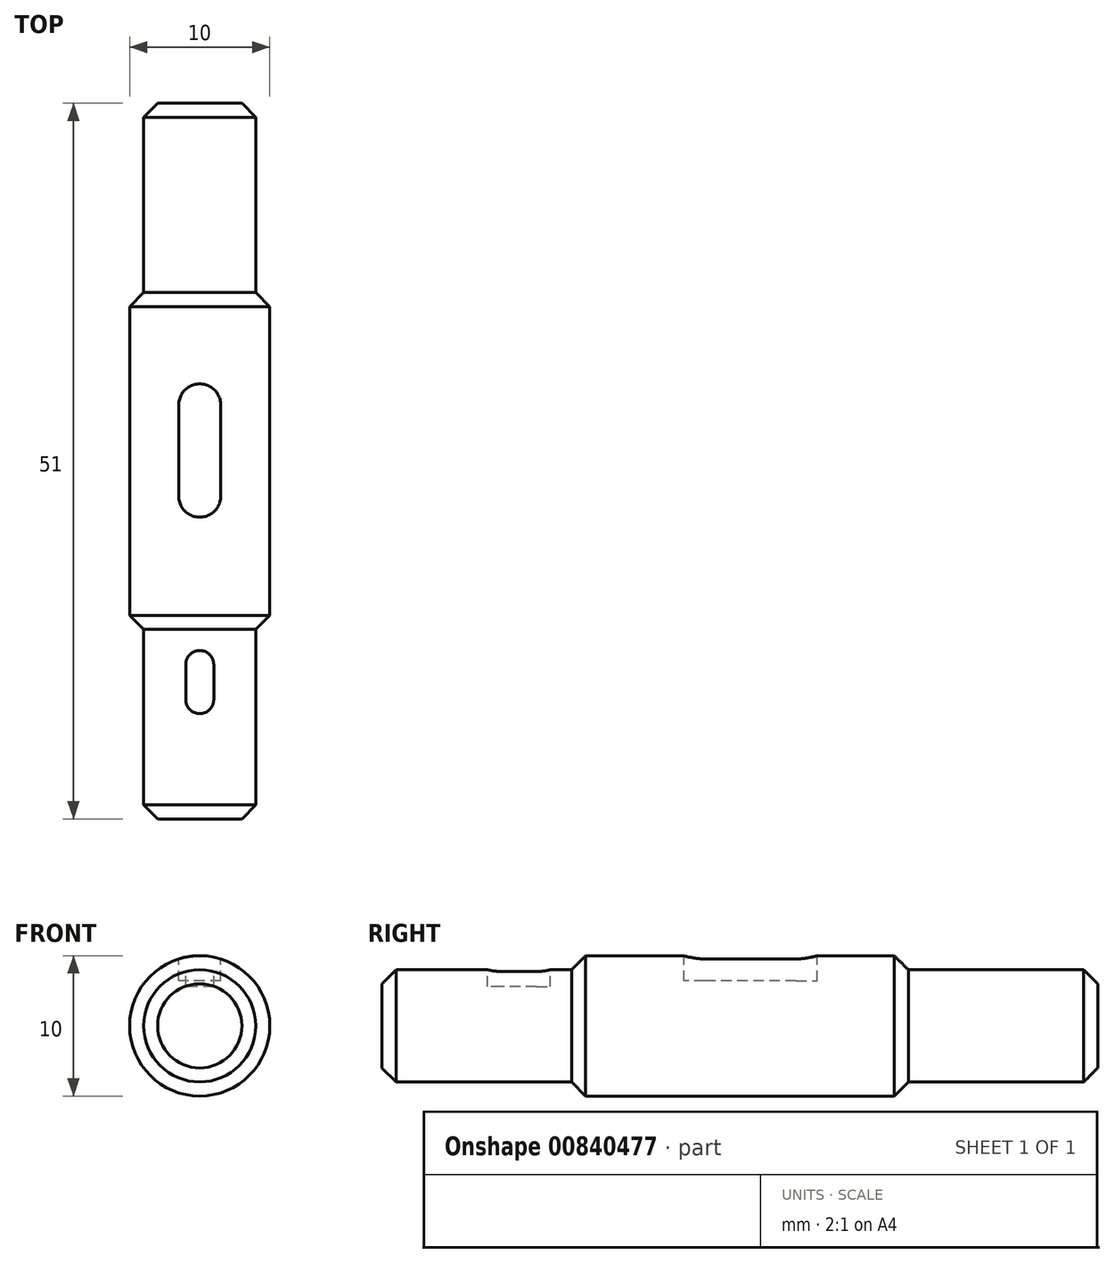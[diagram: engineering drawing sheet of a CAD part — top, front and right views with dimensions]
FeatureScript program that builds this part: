
annotation { "Feature Type Name" : "Feature", "Feature Type Description" : "" }
export const myFeature = defineFeature(function(context is Context, id is Id, definition is map)
    precondition{}
    {
        {
            var Q0;
            Q0=qCreatedBy(makeId("Right.planeOp"),FACE);
            var sketch = newSketch(context, id + "F0", { "sketchPlane" : qUnion([Q0])});
            skLineSegment(sketch, "E0", {"start": v(0, 0) * mm, "end": v(0, 4) * mm});
            skLineSegment(sketch, "E1", {"start": v(0, 4) * mm, "end": v(13.5, 4) * mm});
            skLineSegment(sketch, "E2", {"start": v(13.5, 4) * mm, "end": v(13.5, 5) * mm});
            skLineSegment(sketch, "E3", {"start": v(13.5, 5) * mm, "end": v(37.5, 5) * mm});
            skLineSegment(sketch, "E4", {"start": v(37.5, 5) * mm, "end": v(37.5, 4) * mm});
            skLineSegment(sketch, "E5", {"start": v(37.5, 4) * mm, "end": v(51, 4) * mm});
            skLineSegment(sketch, "E6", {"start": v(51, 4) * mm, "end": v(51, 0) * mm});
            skLineSegment(sketch, "E7", {"start": v(51, 0) * mm, "end": v(0, 0) * mm});
            skSolve(sketch);
        }
        {
            var Q0;
            Q0=makeQuery(id+"F0.imprint","IMPRINT",FACE,{"disambiguationData":[TD([[makeQuery(id+"F0.imprint","IMPRINT",EDGE,{"derivedFrom":sQuery(id+"F0.wireOp",EDGE,"E0")}),-1.0]])]});
            var Q1;
            Q1=sQuery(id+"F0.wireOp",EDGE,"E7");
            revolve(context, id + "F1", {"surfaceOperationType" : NewSurfaceOperationType.NEW, "entities" : qUnion([Q0]), "axis" : qUnion([Q1]), "revolveType" : RevolveType.FULL});
        }
        {
            var Q0;
            Q0=makeQuery(id+"F1.opRevolve","SWEPT_FACE",FACE,{"disambiguationData":[OSD([sQuery(id+"F0.wireOp",EDGE,"E2")])]});
            cPlane(context, id + "F2", {"entities" : qUnion([Q0]), "cplaneType" : CPlaneType.OFFSET, "offset" : 7.5 * mm, "width" : 150 * mm, "height" : 150 * mm});
        }
        {
            var Q0;
            Q0=qCreatedBy(id+"F2.planeOp",FACE);
            var sketch = newSketch(context, id + "F3", { "sketchPlane" : qUnion([Q0])});
            skLineSegment(sketch, "E8", {"start": v(-1, 3.87) * mm, "end": v(-1, 2.8) * mm});
            skLineSegment(sketch, "E9", {"start": v(-1, 2.8) * mm, "end": v(1, 2.8) * mm});
            skLineSegment(sketch, "E10", {"start": v(1, 2.8) * mm, "end": v(1, 3.87) * mm});
            skArc(sketch, "E11.0", {"start": v(1, 3.87) * mm, "mid": v(0, 4) * mm, "end": v(-1, 3.87) * mm});
            skSolve(sketch);
        }
        {
            var Q0;
            Q0=qCreatedBy(makeId("Top.planeOp"),FACE);
            cPlane(context, id + "F4", {"entities" : qUnion([Q0]), "cplaneType" : CPlaneType.OFFSET, "offset" : 4 * mm, "width" : 150 * mm, "height" : 150 * mm});
        }
        {
            var Q0;
            Q0=qCreatedBy(id+"F4.planeOp",FACE);
            var sketch = newSketch(context, id + "F5", { "sketchPlane" : qUnion([Q0])});
            skArc(sketch, "E12", {"start": v(1, 11) * mm, "mid": v(0, 12) * mm, "end": v(-1, 11) * mm});
            skArc(sketch, "E13", {"start": v(-1, 8.5) * mm, "mid": v(0, 7.5) * mm, "end": v(1, 8.5) * mm});
            skLineSegment(sketch, "E14", {"start": v(-1, 11) * mm, "end": v(-1, 8.5) * mm});
            skLineSegment(sketch, "E15", {"start": v(1, 11) * mm, "end": v(1, 8.5) * mm});
            skSolve(sketch);
        }
        {
            var Q0;
            Q0=makeQuery(id+"F5.imprint","IMPRINT",FACE,{"disambiguationData":[TD([[makeQuery(id+"F5.imprint","IMPRINT",EDGE,{"derivedFrom":sQuery(id+"F5.wireOp",EDGE,"E12")}),1.0]])]});
            extrude(context, id + "F6", {"entities" : qUnion([Q0]), "operationType" : NewBodyOperationType.REMOVE, "oppositeDirection" : true, "depth" : 1.2 * mm, "offsetDistance" : 25 * mm});
        }
        {
            var Q0;
            Q0=makeQuery(id+"F1.opRevolve","SWEPT_EDGE",EDGE,{"disambiguationData":[OSD([sQuery(id+"F0.wireOp",EDGE,"E2"),sQuery(id+"F0.wireOp",EDGE,"E3")])]});
            var Q1;
            Q1=makeQuery(id+"F1.opRevolve","SWEPT_EDGE",EDGE,{"disambiguationData":[OSD([sQuery(id+"F0.wireOp",EDGE,"E3"),sQuery(id+"F0.wireOp",EDGE,"E4")])]});
            var Q2;
            Q2=makeQuery(id+"F1.opRevolve","SWEPT_EDGE",EDGE,{"disambiguationData":[OSD([sQuery(id+"F0.wireOp",EDGE,"E5"),sQuery(id+"F0.wireOp",EDGE,"E6")])]});
            var Q3;
            Q3=makeQuery(id+"F1.opRevolve","SWEPT_EDGE",EDGE,{"disambiguationData":[OSD([sQuery(id+"F0.wireOp",EDGE,"E0"),sQuery(id+"F0.wireOp",EDGE,"E1")])]});
            chamfer(context, id + "F7", {"entities" : qUnion([Q0, Q1, Q2, Q3]), "width" : 1 * mm, "tangentPropagation" : true});
        }
        {
            var Q0;
            Q0=makeQuery(id+"F1.opRevolve","SWEPT_FACE",FACE,{"disambiguationData":[OSD([sQuery(id+"F0.wireOp",EDGE,"E0")])]});
            var Q1;
            Q1=makeQuery(id+"F1.opRevolve","SWEPT_FACE",FACE,{"disambiguationData":[OSD([sQuery(id+"F0.wireOp",EDGE,"E6")])]});
            cPlane(context, id + "F8", {"entities" : qUnion([Q0, Q1]), "cplaneType" : CPlaneType.MID_PLANE, "offset" : 25 * mm, "width" : 150 * mm, "height" : 150 * mm});
        }
        {
            var Q0;
            Q0=qCreatedBy(makeId("Top.planeOp"),FACE);
            cPlane(context, id + "F9", {"entities" : qUnion([Q0]), "cplaneType" : CPlaneType.OFFSET, "offset" : 5 * mm, "width" : 150 * mm, "height" : 150 * mm});
        }
        {
            var Q0;
            Q0=qCreatedBy(id+"F9.planeOp",FACE);
            var sketch = newSketch(context, id + "F10", { "sketchPlane" : qUnion([Q0])});
            skArc(sketch, "E16", {"start": v(1.5, 29.5) * mm, "mid": v(0, 31) * mm, "end": v(-1.5, 29.5) * mm});
            skArc(sketch, "E17", {"start": v(-1.5, 23) * mm, "mid": v(0, 21.5) * mm, "end": v(1.5, 23) * mm});
            skLineSegment(sketch, "E18", {"start": v(-1.5, 29.5) * mm, "end": v(-1.5, 23) * mm});
            skLineSegment(sketch, "E19", {"start": v(1.5, 29.5) * mm, "end": v(1.5, 23) * mm});
            skLineSegment(sketch, "E20.0", {"start": v(5, 36.5) * mm, "end": v(-5, 36.5) * mm});
            skLineSegment(sketch, "E21.0", {"start": v(-5, 14.5) * mm, "end": v(5, 14.5) * mm});
            skSolve(sketch);
        }
        {
            var Q0;
            Q0=makeQuery(id+"F10.imprint","IMPRINT",FACE,{"disambiguationData":[TD([[makeQuery(id+"F10.imprint","IMPRINT",EDGE,{"derivedFrom":sQuery(id+"F10.wireOp",EDGE,"E16")}),1.0]])]});
            extrude(context, id + "F11", {"entities" : qUnion([Q0]), "operationType" : NewBodyOperationType.REMOVE, "oppositeDirection" : true, "depth" : 1.8 * mm, "offsetDistance" : 25 * mm});
        }
    });
